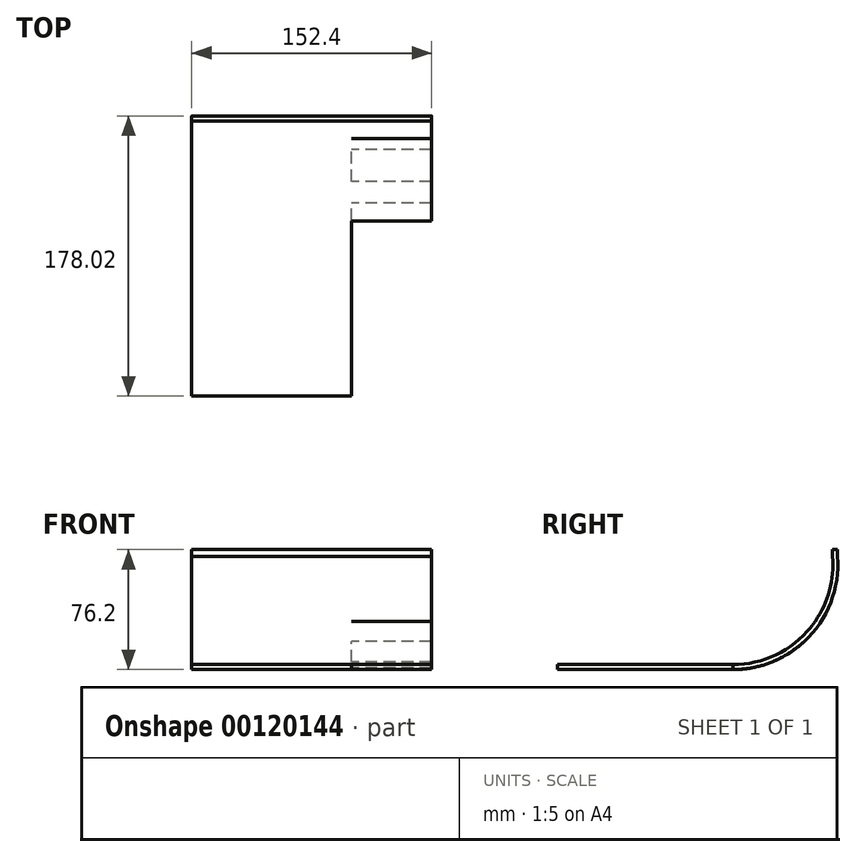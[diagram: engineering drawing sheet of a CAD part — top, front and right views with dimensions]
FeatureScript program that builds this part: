
annotation { "Feature Type Name" : "Feature", "Feature Type Description" : "" }
export const myFeature = defineFeature(function(context is Context, id is Id, definition is map)
    precondition{}
    {
        {
            var Q0;
            Q0=qCreatedBy(makeId("Right.planeOp"),FACE);
            var sketch = newSketch(context, id + "F0", { "sketchPlane" : qUnion([Q0])});
            skLineSegment(sketch, "E0", {"start": v(-111.34, -17.35) * mm, "end": v(0, -17.35) * mm});
            skArc(sketch, "E1", {"start": v(0, -17.35) * mm, "mid": v(49, 4.1) * mm, "end": v(66.46, 54.65) * mm});
            skLineSegment(sketch, "E2", {"start": v(66.46, 54.65) * mm, "end": v(66.46, 58.85) * mm});
            skLineSegment(sketch, "E3.0", {"start": v(63.29, 54.52) * mm, "end": v(63.29, 58.85) * mm});
            skArc(sketch, "E3.1", {"start": v(0, -14.17) * mm, "mid": v(46.7, 6.3) * mm, "end": v(63.29, 54.52) * mm});
            skLineSegment(sketch, "E3.2", {"start": v(-111.34, -14.17) * mm, "end": v(0, -14.17) * mm});
            skLineSegment(sketch, "E4", {"start": v(-111.34, -14.17) * mm, "end": v(-111.34, -17.35) * mm});
            skLineSegment(sketch, "E5", {"start": v(63.29, 58.85) * mm, "end": v(66.46, 58.85) * mm});
            skSolve(sketch);
        }
        {
            var Q0;
            Q0 = qSketchRegion(id + "F0", true);
            extrude(context, id + "F1", {"entities" : qUnion([Q0]), "endBound" : BoundingType.SYMMETRIC, "depth" : 101.6 * mm});
        }
        {
            var Q0;
            Q0=makeQuery(id+"F1.opExtrude","CAP_FACE",FACE,{"disambiguationData":[OSD([sQuery(id+"F0.wireOp",EDGE,"E0"),sQuery(id+"F0.wireOp",EDGE,"E1"),sQuery(id+"F0.wireOp",EDGE,"E2"),sQuery(id+"F0.wireOp",EDGE,"E3.0"),sQuery(id+"F0.wireOp",EDGE,"E3.1"),sQuery(id+"F0.wireOp",EDGE,"E3.2"),sQuery(id+"F0.wireOp",EDGE,"E4"),sQuery(id+"F0.wireOp",EDGE,"E5")])],"isStart":false});
            var sketch = newSketch(context, id + "F2", { "sketchPlane" : qUnion([Q0])});
            skFitSpline(sketch, "E6", {"points": [v(0, -14.17) * mm, v(49.49, 9.54) * mm, v(63.29, 58.85) * mm], "startDerivative": vector(144.2, 8.66) * mm, "endDerivative": vector(14.32, 167.1) * mm});
            skFitSpline(sketch, "E7.0", {"points": [v(0.2, -17.34) * mm, v(6.41, -16.97) * mm, v(17.83, -15.02) * mm, v(29.64, -10.28) * mm, v(37.65, -5.53) * mm, v(42.96, -1.6) * mm, v(47.59, 2.58) * mm, v(50.9, 6.2) * mm, v(53.22, 9.11) * mm, v(55.37, 12.09) * mm, v(57.7, 15.96) * mm, v(60, 21.02) * mm, v(61.84, 26.64) * mm, v(63.32, 32.98) * mm, v(64.93, 42.65) * mm, v(65.85, 51.59) * mm, v(66.45, 58.58) * mm]});
            skLineSegment(sketch, "E8", {"start": v(0.2, -17.34) * mm, "end": v(0, -14.17) * mm});
            skLineSegment(sketch, "E9", {"start": v(63.29, 58.85) * mm, "end": v(66.46, 58.85) * mm});
            skSolve(sketch);
        }
        {
            var Q0;
            Q0 = qSketchRegion(id + "F2", true);
            var Q1;
            {var subQ4=sQuery(id+"F2.wireOp",EDGE,"E8");Q1=makeQuery(id+"F2.imprint","IMPRINT",FACE,{"disambiguationData":[TD([[makeQuery(id+"F2.imprint","IMPRINT",EDGE,{"derivedFrom":subQ4}),-1.0]])]});}
            extrude(context, id + "F3", {"entities" : qUnion([Q0, Q1]), "operationType" : NewBodyOperationType.ADD, "depth" : 50.8 * mm});
        }
    });
